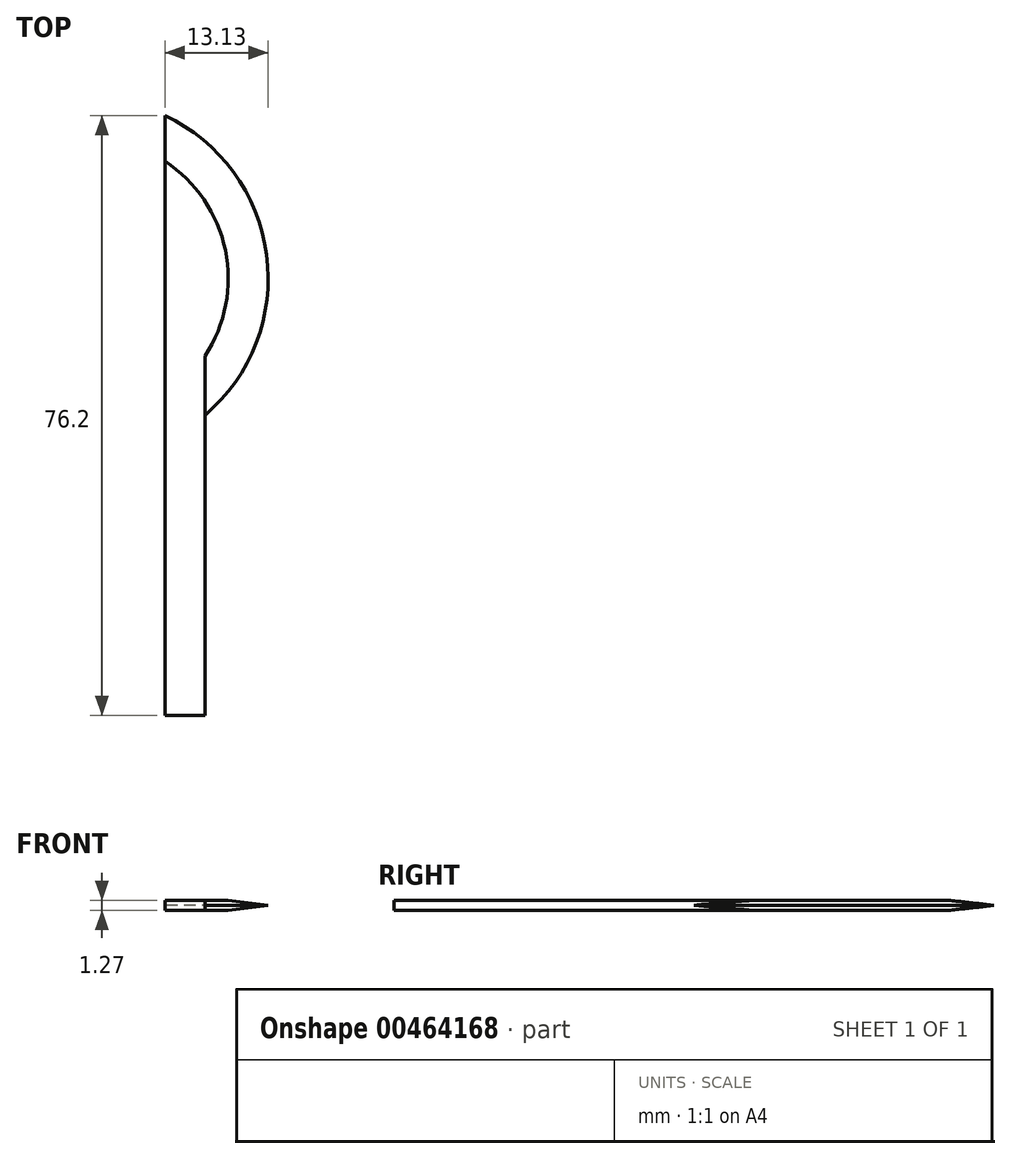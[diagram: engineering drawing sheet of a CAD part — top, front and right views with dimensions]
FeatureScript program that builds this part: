
annotation { "Feature Type Name" : "Feature", "Feature Type Description" : "" }
export const myFeature = defineFeature(function(context is Context, id is Id, definition is map)
    precondition{}
    {
        {
            var Q0;
            Q0=qCreatedBy(makeId("Top.planeOp"),FACE);
            var sketch = newSketch(context, id + "F0", { "sketchPlane" : qUnion([Q0])});
            skLineSegment(sketch, "E0", {"start": v(-36.83, 0) * mm, "end": v(-31.75, 0) * mm});
            skLineSegment(sketch, "E1", {"start": v(-36.83, 0) * mm, "end": v(-36.83, 25.4) * mm});
            skLineSegment(sketch, "E2", {"start": v(-31.75, 0) * mm, "end": v(-31.75, 25.4) * mm});
            skLineSegment(sketch, "E3", {"start": v(-31.75, 25.4) * mm, "end": v(-31.75, 38.1) * mm});
            skLineSegment(sketch, "E4", {"start": v(-36.83, 25.4) * mm, "end": v(-36.83, 76.2) * mm});
            skArc(sketch, "E5", {"start": v(-31.75, 38.1) * mm, "mid": v(-23.9, 58.54) * mm, "end": v(-36.83, 76.2) * mm});
            skSolve(sketch);
        }
        {
            var Q0;
            Q0=makeQuery(id+"F0.imprint","IMPRINT",FACE,{"disambiguationData":[TD([[makeQuery(id+"F0.imprint","IMPRINT",EDGE,{"derivedFrom":sQuery(id+"F0.wireOp",EDGE,"E0")}),1.0]])]});
            extrude(context, id + "F1", {"entities" : qUnion([Q0]), "depth" : 1.27 * mm});
        }
        {
            var Q0;
            Q0=makeQuery(id+"F1.opExtrude","CAP_EDGE",EDGE,{"disambiguationData":[OSD([sQuery(id+"F0.wireOp",EDGE,"E5")])],"isStart":false});
            chamfer(context, id + "F2", {"entities" : qUnion([Q0]), "chamferType" : ChamferType.TWO_OFFSETS, "width1" : 5.08 * mm, "oppositeDirection" : false, "width2" : 0.64 * mm, "tangentPropagation" : true});
        }
        {
            var Q0;
            Q0=makeQuery(id+"F1.opExtrude","CAP_EDGE",EDGE,{"disambiguationData":[OSD([sQuery(id+"F0.wireOp",EDGE,"E5")])],"isStart":true});
            chamfer(context, id + "F3", {"entities" : qUnion([Q0]), "chamferType" : ChamferType.TWO_OFFSETS, "width1" : 0.64 * mm, "oppositeDirection" : false, "width2" : 5.08 * mm, "tangentPropagation" : true});
        }
    });
